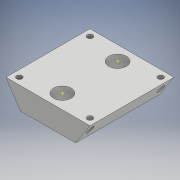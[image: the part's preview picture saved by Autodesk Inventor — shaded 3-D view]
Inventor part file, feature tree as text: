
AUTODESK INVENTOR PART (.ipt)
format: ipt  version: 2017 (Build 210142000, 142)  size: 141,824 bytes
history: native  units: mm
features: hole x3, sketch x3, extrude x2, other x2
ambient origin geometry x8: Origin, YZ Plane, XZ Plane, XY Plane, X Axis, Y Axis, Z Axis, Center Point
bodies: Solid1 (feature_tree)
feature tree (10):
  extrude  "Extrusion1"  Depth=38.0mm
  extrude  "Extrusion2"  Depth=4.2mm
  hole  "Hole1"  [1 undecoded]
  other  "Work Point1"
  other  "Work Point2"
  hole  "Hole2"  [1 undecoded]
  hole  "Hole3"  [1 undecoded]
  sketch  "Sketch1"  dims[d0=25.0mm d1=38.0mm]
  sketch  "Sketch2"  dims[d2=4.2mm d3=4.2mm]
  sketch  "Sketch3"  dims[d4=12.5mm d5=12.5mm d6=10.0mm d7=0.0mm d8=6.5mm d9=6.5mm d10=30.0mm d11=0.0mm d12=16.0mm d13=16.0mm d14=20.0mm d16=32.0mm d17=20.0mm d19=32.0mm d22=2.5mm d23=6.0mm d24=4.0mm d25=2.0mm d26=90.0deg d27=20.0mm d28=20.594885mm d47=10.0mm d48=10.0mm d31=8.0mm d32=6.0mm d33=4.0mm d34=2.0mm d35=90.0deg d36=6.0mm d37=20.594885mm d49=10.0mm d50=10.0mm d40=8.0mm d41=6.0mm d42=4.0mm d43=2.0mm d44=90.0deg d45=6.0mm d46=20.594885mm]
note: 3 required parameter values undecoded (feature->parameter linkage not recoverable at this tier; creation-order binding heuristic only, values carry confidence <= 0.55)
